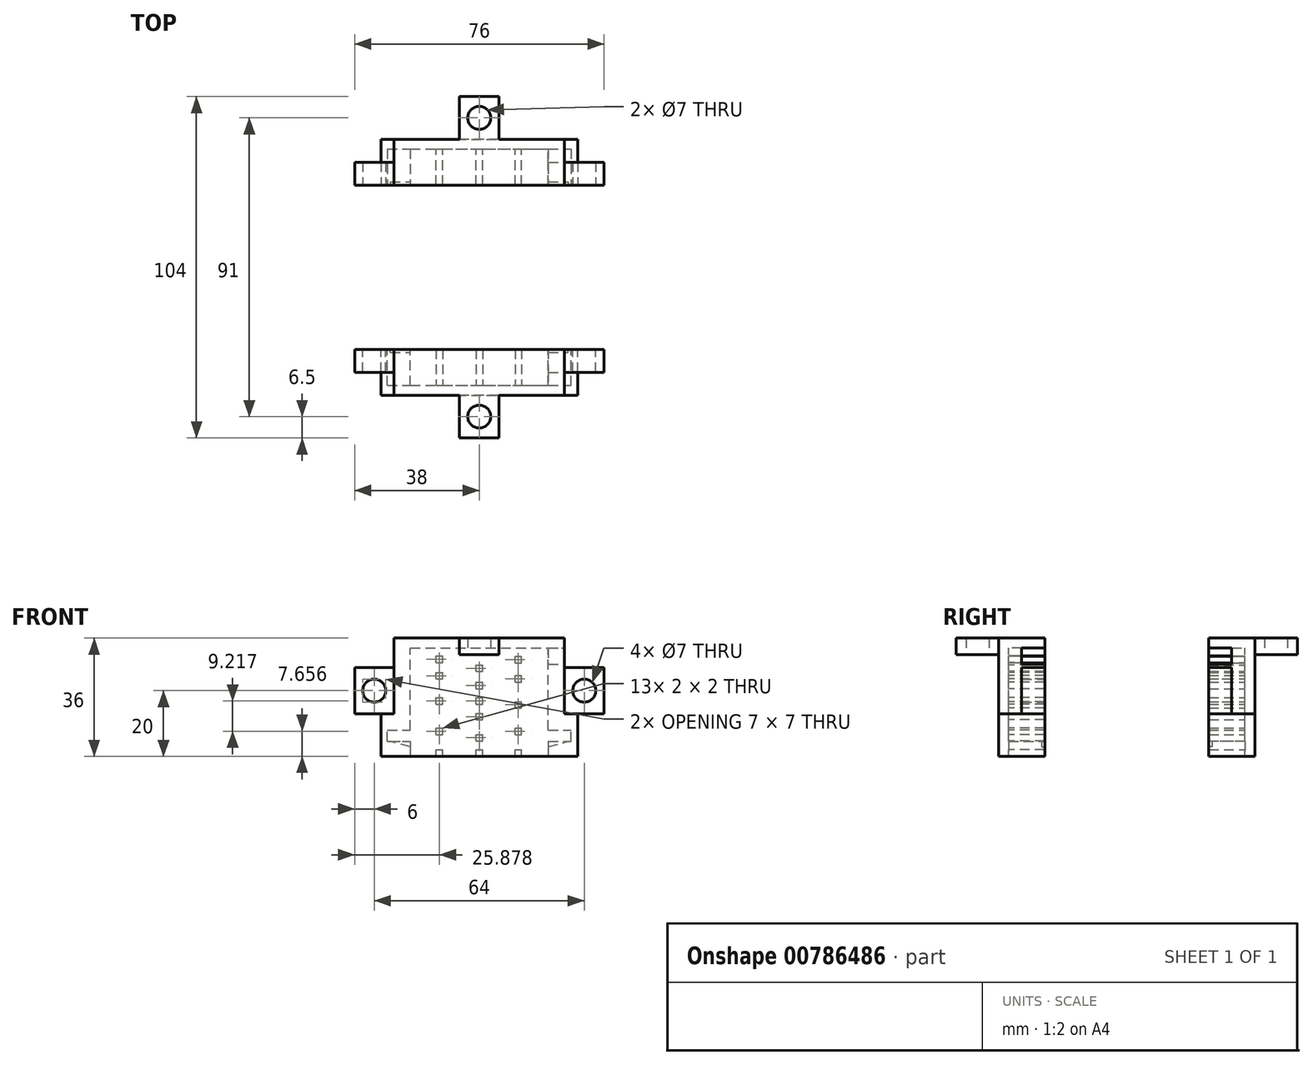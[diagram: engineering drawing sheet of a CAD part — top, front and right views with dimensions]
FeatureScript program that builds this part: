
annotation { "Feature Type Name" : "Feature", "Feature Type Description" : "" }
export const myFeature = defineFeature(function(context is Context, id is Id, definition is map)
    precondition{}
    {
        {
            var Q0;
            Q0=qCreatedBy(makeId("Top.planeOp"),FACE);
            var sketch = newSketch(context, id + "F0", { "sketchPlane" : qUnion([Q0])});
            skLineSegment(sketch, "E0.bottom", {"start": v(-30, 7) * mm, "end": v(30, 7) * mm});
            skLineSegment(sketch, "E0.top", {"start": v(-30, -7) * mm, "end": v(30, -7) * mm});
            skLineSegment(sketch, "E0.left", {"start": v(-30, 7) * mm, "end": v(-30, -7) * mm});
            skLineSegment(sketch, "E0.right", {"start": v(30, 7) * mm, "end": v(30, -7) * mm});
            skSolve(sketch);
        }
        {
            var Q0;
            Q0 = qSketchRegion(id + "F0", true);
            extrude(context, id + "F1", {"entities" : qUnion([Q0]), "depth" : 36 * mm, "offsetDistance" : 25 * mm});
        }
        {
            var Q0;
            Q0=makeQuery(id+"F1.opExtrude","CAP_FACE",FACE,{"disambiguationData":[OSD([sQuery(id+"F0.wireOp",EDGE,"E0.bottom"),sQuery(id+"F0.wireOp",EDGE,"E0.top"),sQuery(id+"F0.wireOp",EDGE,"E0.left"),sQuery(id+"F0.wireOp",EDGE,"E0.right")])],"isStart":false});
            cPlane(context, id + "F2", {"entities" : qUnion([Q0]), "cplaneType" : CPlaneType.OFFSET, "offset" : 3 * mm, "oppositeDirection" : true, "width" : 150 * mm, "height" : 150 * mm});
        }
        {
            var Q0;
            Q0=qCreatedBy(id+"F2.planeOp",FACE);
            var sketch = newSketch(context, id + "F3", { "sketchPlane" : qUnion([Q0])});
            skLineSegment(sketch, "E1.bottom", {"start": v(-21, 7) * mm, "end": v(21, 7) * mm});
            skLineSegment(sketch, "E1.top", {"start": v(-21, -4) * mm, "end": v(21, -4) * mm});
            skLineSegment(sketch, "E1.left", {"start": v(-21, 7) * mm, "end": v(-21, -4) * mm});
            skLineSegment(sketch, "E1.right", {"start": v(21, 7) * mm, "end": v(21, -4) * mm});
            skSolve(sketch);
        }
        {
            var Q0;
            Q0 = qSketchRegion(id + "F3", true);
            extrude(context, id + "F4", {"entities" : qUnion([Q0]), "operationType" : NewBodyOperationType.REMOVE, "oppositeDirection" : true, "depth" : 25 * mm, "offsetDistance" : 25 * mm});
        }
        {
            var Q0;
            Q0=makeQuery(id+"F1.opExtrude","SWEPT_FACE",FACE,{"disambiguationData":[OSD([sQuery(id+"F0.wireOp",EDGE,"E0.bottom")])]});
            var sketch = newSketch(context, id + "F5", { "sketchPlane" : qUnion([Q0])});
            skLineSegment(sketch, "E2.bottom", {"start": v(28, 4.5) * mm, "end": v(-28, 4.5) * mm});
            skLineSegment(sketch, "E2.top", {"start": v(28, 8) * mm, "end": v(-28, 8) * mm});
            skLineSegment(sketch, "E2.left", {"start": v(28, 4.5) * mm, "end": v(28, 8) * mm});
            skLineSegment(sketch, "E2.right", {"start": v(-28, 4.5) * mm, "end": v(-28, 8) * mm});
            skLineSegment(sketch, "E3.bottom", {"start": v(21, 4.5) * mm, "end": v(-21, 4.5) * mm});
            skLineSegment(sketch, "E3.top", {"start": v(21, 0) * mm, "end": v(-21, 0) * mm});
            skLineSegment(sketch, "E3.left", {"start": v(21, 4.5) * mm, "end": v(21, 0) * mm});
            skLineSegment(sketch, "E3.right", {"start": v(-21, 4.5) * mm, "end": v(-21, 0) * mm});
            skSolve(sketch);
        }
        {
            var Q0;
            {var subQ9=sQuery(id+"F5.wireOp",EDGE,"E2.left");Q0=qUnion([makeQuery(id+"F5.imprint","IMPRINT",FACE,{"disambiguationData":[TD([[makeQuery(id+"F5.imprint","IMPRINT",EDGE,{"derivedFrom":subQ9}),1.0]])]}),makeQuery(id+"F5.imprint","IMPRINT",FACE,{"disambiguationData":[TD([[makeQuery(id+"F5.imprint","IMPRINT",EDGE,{"derivedFrom":sQuery(id+"F5.wireOp",EDGE,"E3.top")}),-1.0]])]})]);}
            extrude(context, id + "F6", {"entities" : qUnion([Q0]), "operationType" : NewBodyOperationType.REMOVE, "oppositeDirection" : true, "depth" : 11 * mm, "offsetDistance" : 25 * mm});
        }
        {
            var Q0;
            Q0=makeQuery(id+"F1.opExtrude","SWEPT_FACE",FACE,{"disambiguationData":[OSD([sQuery(id+"F0.wireOp",EDGE,"E0.bottom")])]});
            var sketch = newSketch(context, id + "F7", { "sketchPlane" : qUnion([Q0])});
            skLineSegment(sketch, "E4.bottom", {"start": v(30, 13) * mm, "end": v(38, 13) * mm});
            skLineSegment(sketch, "E4.top", {"start": v(30, 27) * mm, "end": v(38, 27) * mm});
            skLineSegment(sketch, "E4.left", {"start": v(30, 13) * mm, "end": v(30, 27) * mm});
            skLineSegment(sketch, "E4.right", {"start": v(38, 13) * mm, "end": v(38, 27) * mm});
            skLineSegment(sketch, "E5.MirrorCS", {"start": v(-38, 13) * mm, "end": v(-38, 27) * mm});
            skLineSegment(sketch, "E6.MirrorCS", {"start": v(-30, 13) * mm, "end": v(-38, 13) * mm});
            skLineSegment(sketch, "E7.MirrorCS", {"start": v(-30, 13) * mm, "end": v(-30, 27) * mm});
            skLineSegment(sketch, "E8.MirrorCS", {"start": v(-30, 27) * mm, "end": v(-38, 27) * mm});
            skSolve(sketch);
        }
        {
            var Q0;
            Q0 = qSketchRegion(id + "F7", true);
            extrude(context, id + "F8", {"entities" : qUnion([Q0]), "operationType" : NewBodyOperationType.ADD, "oppositeDirection" : true, "depth" : 14 * mm, "offsetDistance" : 25 * mm});
        }
        {
            var Q0;
            Q0=makeQuery(id+"F8.boolean.opBoolean","MERGE",FACE,{"derivedFrom":[makeQuery(id+"F1.opExtrude","SWEPT_FACE",FACE,{"disambiguationData":[OSD([sQuery(id+"F0.wireOp",EDGE,"E0.bottom")])]}),makeQuery(id+"F8.opExtrude","CAP_FACE",FACE,{"disambiguationData":[OSD([sQuery(id+"F7.wireOp",EDGE,"E4.bottom"),sQuery(id+"F7.wireOp",EDGE,"E4.top"),sQuery(id+"F7.wireOp",EDGE,"E4.left"),sQuery(id+"F7.wireOp",EDGE,"E4.right")])],"isStart":true}),makeQuery(id+"F8.opExtrude","CAP_FACE",FACE,{"disambiguationData":[OSD([sQuery(id+"F7.wireOp",EDGE,"E5.MirrorCS"),sQuery(id+"F7.wireOp",EDGE,"E6.MirrorCS"),sQuery(id+"F7.wireOp",EDGE,"E7.MirrorCS"),sQuery(id+"F7.wireOp",EDGE,"E8.MirrorCS")])],"isStart":true})]});
            var sketch = newSketch(context, id + "F9", { "sketchPlane" : qUnion([Q0])});
            skCircle(sketch, "E9", {"center": v(32, 20) * mm, "radius": 3.5 * mm});
            skCircle(sketch, "E10.MirrorC", {"center": v(-32, 20) * mm, "radius": 3.5 * mm});
            skSolve(sketch);
        }
        {
            var Q0;
            Q0 = qSketchRegion(id + "F9", true);
            extrude(context, id + "F10", {"entities" : qUnion([Q0]), "operationType" : NewBodyOperationType.REMOVE, "oppositeDirection" : true, "depth" : 14 * mm, "offsetDistance" : 25 * mm});
        }
        {
            var Q0;
            Q0=makeQuery(id+"F8.boolean.opBoolean","MERGE",FACE,{"derivedFrom":[makeQuery(id+"F1.opExtrude","SWEPT_FACE",FACE,{"disambiguationData":[OSD([sQuery(id+"F0.wireOp",EDGE,"E0.top")])]}),makeQuery(id+"F8.opExtrude","CAP_FACE",FACE,{"disambiguationData":[OSD([sQuery(id+"F7.wireOp",EDGE,"E4.bottom"),sQuery(id+"F7.wireOp",EDGE,"E4.top"),sQuery(id+"F7.wireOp",EDGE,"E4.left"),sQuery(id+"F7.wireOp",EDGE,"E4.right")])],"isStart":false}),makeQuery(id+"F8.opExtrude","CAP_FACE",FACE,{"disambiguationData":[OSD([sQuery(id+"F7.wireOp",EDGE,"E5.MirrorCS"),sQuery(id+"F7.wireOp",EDGE,"E6.MirrorCS"),sQuery(id+"F7.wireOp",EDGE,"E7.MirrorCS"),sQuery(id+"F7.wireOp",EDGE,"E8.MirrorCS")])],"isStart":false})]});
            var sketch = newSketch(context, id + "F11", { "sketchPlane" : qUnion([Q0])});
            skLineSegment(sketch, "E11.bottom", {"start": v(38, 13) * mm, "end": v(26, 13) * mm});
            skLineSegment(sketch, "E11.top", {"start": v(38, 27) * mm, "end": v(26, 27) * mm});
            skLineSegment(sketch, "E11.left", {"start": v(38, 13) * mm, "end": v(38, 27) * mm});
            skLineSegment(sketch, "E11.right", {"start": v(26, 13) * mm, "end": v(26, 27) * mm});
            skLineSegment(sketch, "E12.MirrorCS", {"start": v(-38, 13) * mm, "end": v(-26, 13) * mm});
            skLineSegment(sketch, "E13.MirrorCS", {"start": v(-26, 13) * mm, "end": v(-26, 27) * mm});
            skLineSegment(sketch, "E14.MirrorCS", {"start": v(-38, 13) * mm, "end": v(-38, 27) * mm});
            skLineSegment(sketch, "E15.MirrorCS", {"start": v(-38, 27) * mm, "end": v(-26, 27) * mm});
            skSolve(sketch);
        }
        {
            var Q0;
            Q0 = qSketchRegion(id + "F11", true);
            extrude(context, id + "F12", {"entities" : qUnion([Q0]), "operationType" : NewBodyOperationType.REMOVE, "oppositeDirection" : true, "depth" : 7 * mm, "offsetDistance" : 25 * mm});
        }
        {
            var Q0;
            Q0=makeQuery(id+"F8.boolean.opBoolean","MERGE",FACE,{"derivedFrom":[makeQuery(id+"F1.opExtrude","SWEPT_FACE",FACE,{"disambiguationData":[OSD([sQuery(id+"F0.wireOp",EDGE,"E0.top")])]}),makeQuery(id+"F8.opExtrude","CAP_FACE",FACE,{"disambiguationData":[OSD([sQuery(id+"F7.wireOp",EDGE,"E4.bottom"),sQuery(id+"F7.wireOp",EDGE,"E4.top"),sQuery(id+"F7.wireOp",EDGE,"E4.left"),sQuery(id+"F7.wireOp",EDGE,"E4.right")])],"isStart":false}),makeQuery(id+"F8.opExtrude","CAP_FACE",FACE,{"disambiguationData":[OSD([sQuery(id+"F7.wireOp",EDGE,"E5.MirrorCS"),sQuery(id+"F7.wireOp",EDGE,"E6.MirrorCS"),sQuery(id+"F7.wireOp",EDGE,"E7.MirrorCS"),sQuery(id+"F7.wireOp",EDGE,"E8.MirrorCS")])],"isStart":false})]});
            var sketch = newSketch(context, id + "F13", { "sketchPlane" : qUnion([Q0])});
            skLineSegment(sketch, "E16.bottom", {"start": v(30, 36) * mm, "end": v(26, 36) * mm});
            skLineSegment(sketch, "E16.top", {"start": v(30, 27) * mm, "end": v(26, 27) * mm});
            skLineSegment(sketch, "E16.left", {"start": v(30, 36) * mm, "end": v(30, 27) * mm});
            skLineSegment(sketch, "E16.right", {"start": v(26, 36) * mm, "end": v(26, 27) * mm});
            skLineSegment(sketch, "E17.bottom", {"start": v(-30, 36) * mm, "end": v(-26, 36) * mm});
            skLineSegment(sketch, "E17.top", {"start": v(-30, 27) * mm, "end": v(-26, 27) * mm});
            skLineSegment(sketch, "E17.left", {"start": v(-30, 36) * mm, "end": v(-30, 27) * mm});
            skLineSegment(sketch, "E17.right", {"start": v(-26, 36) * mm, "end": v(-26, 27) * mm});
            skSolve(sketch);
        }
        {
            var Q0;
            Q0 = qSketchRegion(id + "F13", true);
            extrude(context, id + "F14", {"entities" : qUnion([Q0]), "operationType" : NewBodyOperationType.REMOVE, "oppositeDirection" : true, "depth" : 14 * mm, "offsetDistance" : 25 * mm});
        }
        {
            var Q0;
            Q0=makeQuery(id+"F14.boolean.opBoolean","MERGE",FACE,{"derivedFrom":[makeQuery(id+"F12.boolean.opBoolean","COPY",FACE,{"derivedFrom":makeQuery(id+"F12.opExtrude","SWEPT_FACE",FACE,{"disambiguationData":[OSD([sQuery(id+"F11.wireOp",EDGE,"E11.right")])]})}),makeQuery(id+"F14.opExtrude","SWEPT_FACE",FACE,{"disambiguationData":[OSD([sQuery(id+"F13.wireOp",EDGE,"E16.right")])]})]});
            var sketch = newSketch(context, id + "F15", { "sketchPlane" : qUnion([Q0])});
            skLineSegment(sketch, "E18.bottom", {"start": v(7, 33) * mm, "end": v(0, 33) * mm});
            skLineSegment(sketch, "E18.top", {"start": v(7, 28) * mm, "end": v(0, 28) * mm});
            skLineSegment(sketch, "E18.left", {"start": v(7, 33) * mm, "end": v(7, 28) * mm});
            skLineSegment(sketch, "E18.right", {"start": v(0, 33) * mm, "end": v(0, 28) * mm});
            skSolve(sketch);
        }
        {
            var Q0;
            Q0 = qSketchRegion(id + "F15", true);
            extrude(context, id + "F16", {"entities" : qUnion([Q0]), "operationType" : NewBodyOperationType.REMOVE, "oppositeDirection" : true, "depth" : 5 * mm, "offsetDistance" : 25 * mm});
        }
        {
            var Q0;
            {var subQ0=sQuery(id+"F7.wireOp",EDGE,"E8.MirrorCS");var subQ1=sQuery(id+"F7.wireOp",EDGE,"E5.MirrorCS");var subQ3=sQuery(id+"F0.wireOp",EDGE,"E0.bottom");var subQ4=makeQuery(id+"F1.opExtrude","SWEPT_FACE",FACE,{"disambiguationData":[OSD([subQ3])]});var subQ10=sQuery(id+"F0.wireOp",EDGE,"E0.right");var subQ11=sQuery(id+"F7.wireOp",EDGE,"E6.MirrorCS");Q0=makeQuery(id+"F16.boolean.opBoolean","SPLIT",FACE,{"disambiguationData":[TD([makeQuery(id+"F1.opExtrude","SWEPT_FACE",FACE,{"disambiguationData":[OSD([subQ10])]})])],"derivedFrom":makeQuery(id+"F8.boolean.opBoolean","MERGE",FACE,{"derivedFrom":[subQ4,makeQuery(id+"F8.opExtrude","CAP_FACE",FACE,{"disambiguationData":[OSD([sQuery(id+"F7.wireOp",EDGE,"E4.bottom"),sQuery(id+"F7.wireOp",EDGE,"E4.top"),sQuery(id+"F7.wireOp",EDGE,"E4.left"),sQuery(id+"F7.wireOp",EDGE,"E4.right")])],"isStart":true}),makeQuery(id+"F8.opExtrude","CAP_FACE",FACE,{"disambiguationData":[OSD([subQ1,subQ11,sQuery(id+"F7.wireOp",EDGE,"E7.MirrorCS"),subQ0])],"isStart":true})]})});}
            var sketch = newSketch(context, id + "F17", { "sketchPlane" : qUnion([Q0])});
            skLineSegment(sketch, "E19", {"start": v(-21, 2.86) * mm, "end": v(-27.1, 4.5) * mm});
            skLineSegment(sketch, "E20", {"start": v(-27.1, 4.5) * mm, "end": v(-21, 4.5) * mm});
            skLineSegment(sketch, "E21", {"start": v(-21, 4.5) * mm, "end": v(-21, 2.86) * mm});
            skLineSegment(sketch, "E22.MirrorCS", {"start": v(21, 2.86) * mm, "end": v(27.1, 4.5) * mm});
            skLineSegment(sketch, "E23.MirrorCS", {"start": v(21, 4.5) * mm, "end": v(21, 2.86) * mm});
            skLineSegment(sketch, "E24.MirrorCS", {"start": v(27.1, 4.5) * mm, "end": v(21, 4.5) * mm});
            skSolve(sketch);
        }
        {
            var Q0;
            Q0 = qSketchRegion(id + "F17", true);
            extrude(context, id + "F18", {"entities" : qUnion([Q0]), "operationType" : NewBodyOperationType.REMOVE, "oppositeDirection" : true, "depth" : 1 * mm, "offsetDistance" : 25 * mm});
        }
        {
            var Q0;
            Q0=makeQuery(id+"F8.boolean.opBoolean","MERGE",FACE,{"derivedFrom":[makeQuery(id+"F1.opExtrude","SWEPT_FACE",FACE,{"disambiguationData":[OSD([sQuery(id+"F0.wireOp",EDGE,"E0.top")])]}),makeQuery(id+"F8.opExtrude","CAP_FACE",FACE,{"disambiguationData":[OSD([sQuery(id+"F7.wireOp",EDGE,"E4.bottom"),sQuery(id+"F7.wireOp",EDGE,"E4.top"),sQuery(id+"F7.wireOp",EDGE,"E4.left"),sQuery(id+"F7.wireOp",EDGE,"E4.right")])],"isStart":false}),makeQuery(id+"F8.opExtrude","CAP_FACE",FACE,{"disambiguationData":[OSD([sQuery(id+"F7.wireOp",EDGE,"E5.MirrorCS"),sQuery(id+"F7.wireOp",EDGE,"E6.MirrorCS"),sQuery(id+"F7.wireOp",EDGE,"E7.MirrorCS"),sQuery(id+"F7.wireOp",EDGE,"E8.MirrorCS")])],"isStart":false})]});
            var sketch = newSketch(context, id + "F19", { "sketchPlane" : qUnion([Q0])});
            skLineSegment(sketch, "E25.bottom", {"start": v(6, 36) * mm, "end": v(-6, 36) * mm});
            skLineSegment(sketch, "E25.top", {"start": v(6, 31) * mm, "end": v(-6, 31) * mm});
            skLineSegment(sketch, "E25.left", {"start": v(6, 36) * mm, "end": v(6, 31) * mm});
            skLineSegment(sketch, "E25.right", {"start": v(-6, 36) * mm, "end": v(-6, 31) * mm});
            skSolve(sketch);
        }
        {
            var Q0;
            Q0 = qSketchRegion(id + "F19", true);
            extrude(context, id + "F20", {"entities" : qUnion([Q0]), "operationType" : NewBodyOperationType.ADD, "depth" : 13 * mm, "offsetDistance" : 25 * mm});
        }
        {
            var Q0;
            Q0=makeQuery(id+"F20.opExtrude","SWEPT_FACE",FACE,{"disambiguationData":[OSD([sQuery(id+"F19.wireOp",EDGE,"E25.top")])]});
            var sketch = newSketch(context, id + "F21", { "sketchPlane" : qUnion([Q0])});
            skCircle(sketch, "E26", {"center": v(0, 13.5) * mm, "radius": 3.5 * mm});
            skPoint(sketch, "E26.centerSnap0", {"position": v(6, 13.5) * mm});
            skSolve(sketch);
        }
        {
            var Q0;
            Q0 = qSketchRegion(id + "F21", true);
            extrude(context, id + "F22", {"entities" : qUnion([Q0]), "operationType" : NewBodyOperationType.REMOVE, "oppositeDirection" : true, "depth" : 5 * mm, "offsetDistance" : 25 * mm});
        }
        {
            var Q0;
            {var subQ0=sQuery(id+"F7.wireOp",EDGE,"E8.MirrorCS");var subQ1=sQuery(id+"F7.wireOp",EDGE,"E5.MirrorCS");var subQ3=sQuery(id+"F0.wireOp",EDGE,"E0.bottom");var subQ4=makeQuery(id+"F1.opExtrude","SWEPT_FACE",FACE,{"disambiguationData":[OSD([subQ3])]});var subQ10=sQuery(id+"F0.wireOp",EDGE,"E0.right");var subQ11=sQuery(id+"F7.wireOp",EDGE,"E6.MirrorCS");Q0=makeQuery(id+"F16.boolean.opBoolean","SPLIT",FACE,{"disambiguationData":[TD([makeQuery(id+"F1.opExtrude","SWEPT_FACE",FACE,{"disambiguationData":[OSD([subQ10])]})])],"derivedFrom":makeQuery(id+"F8.boolean.opBoolean","MERGE",FACE,{"derivedFrom":[subQ4,makeQuery(id+"F8.opExtrude","CAP_FACE",FACE,{"disambiguationData":[OSD([sQuery(id+"F7.wireOp",EDGE,"E4.bottom"),sQuery(id+"F7.wireOp",EDGE,"E4.top"),sQuery(id+"F7.wireOp",EDGE,"E4.left"),sQuery(id+"F7.wireOp",EDGE,"E4.right")])],"isStart":true}),makeQuery(id+"F8.opExtrude","CAP_FACE",FACE,{"disambiguationData":[OSD([subQ1,subQ11,sQuery(id+"F7.wireOp",EDGE,"E7.MirrorCS"),subQ0])],"isStart":true})]})});}
            cPlane(context, id + "F23", {"entities" : qUnion([Q0]), "cplaneType" : CPlaneType.OFFSET, "offset" : 25 * mm, "width" : 150 * mm, "height" : 150 * mm});
        }
        {
            var Q0;
            Q0=makeQuery(id+"F1.opExtrude","SWEPT_BODY",BODY,{"disambiguationData":[OSD([sQuery(id+"F0.wireOp",EDGE,"E0.bottom"),sQuery(id+"F0.wireOp",EDGE,"E0.top"),sQuery(id+"F0.wireOp",EDGE,"E0.left"),sQuery(id+"F0.wireOp",EDGE,"E0.right")])]});
            var Q1;
            Q1=qCreatedBy(id+"F23.planeOp",FACE);
            mirror(context, id + "F24", {"entities" : qUnion([Q0]), "mirrorPlane" : qUnion([Q1])});
        }
        {
            var Q0;
            Q0=makeQuery(id+"F6.boolean.opBoolean","MERGE",FACE,{"derivedFrom":[makeQuery(id+"F4.boolean.opBoolean","COPY",FACE,{"derivedFrom":makeQuery(id+"F4.opExtrude","SWEPT_FACE",FACE,{"disambiguationData":[OSD([sQuery(id+"F3.wireOp",EDGE,"E1.top")])]})})],"fromTools":[makeQuery(id+"F6.opExtrude","CAP_FACE",FACE,{"disambiguationData":[OSD([sQuery(id+"F5.wireOp",EDGE,"E2.bottom"),sQuery(id+"F5.wireOp",EDGE,"E2.top"),sQuery(id+"F5.wireOp",EDGE,"E2.left"),sQuery(id+"F5.wireOp",EDGE,"E2.right"),sQuery(id+"F5.wireOp",EDGE,"E3.top"),sQuery(id+"F5.wireOp",EDGE,"E3.left"),sQuery(id+"F5.wireOp",EDGE,"E3.right")])],"isStart":false})]});
            var sketch = newSketch(context, id + "F25", { "sketchPlane" : qUnion([Q0])});
            skLineSegment(sketch, "E27.bottom", {"start": v(1, 0) * mm, "end": v(-1, 0) * mm});
            skLineSegment(sketch, "E27.top", {"start": v(1, 2) * mm, "end": v(-1, 2) * mm});
            skLineSegment(sketch, "E27.left", {"start": v(1, 0) * mm, "end": v(1, 2) * mm});
            skLineSegment(sketch, "E27.right", {"start": v(-1, 0) * mm, "end": v(-1, 2) * mm});
            skLineSegment(sketch, "E28.bottom", {"start": v(1, 4.66) * mm, "end": v(-1, 4.66) * mm});
            skLineSegment(sketch, "E28.top", {"start": v(1, 6.66) * mm, "end": v(-1, 6.66) * mm});
            skLineSegment(sketch, "E28.left", {"start": v(1, 4.66) * mm, "end": v(1, 6.66) * mm});
            skLineSegment(sketch, "E28.right", {"start": v(-1, 4.66) * mm, "end": v(-1, 6.66) * mm});
            skLineSegment(sketch, "E29.bottom", {"start": v(1, 11.11) * mm, "end": v(-1, 11.11) * mm});
            skLineSegment(sketch, "E29.top", {"start": v(1, 13.11) * mm, "end": v(-1, 13.11) * mm});
            skLineSegment(sketch, "E29.left", {"start": v(1, 11.11) * mm, "end": v(1, 13.11) * mm});
            skLineSegment(sketch, "E29.right", {"start": v(-1, 11.11) * mm, "end": v(-1, 13.11) * mm});
            skLineSegment(sketch, "E30.bottom", {"start": v(1, 15.92) * mm, "end": v(-1, 15.92) * mm});
            skLineSegment(sketch, "E30.top", {"start": v(1, 17.92) * mm, "end": v(-1, 17.92) * mm});
            skLineSegment(sketch, "E30.left", {"start": v(1, 15.92) * mm, "end": v(1, 17.92) * mm});
            skLineSegment(sketch, "E30.right", {"start": v(-1, 15.92) * mm, "end": v(-1, 17.92) * mm});
            skLineSegment(sketch, "E31.bottom", {"start": v(1, 20.57) * mm, "end": v(-1, 20.57) * mm});
            skLineSegment(sketch, "E31.top", {"start": v(1, 22.57) * mm, "end": v(-1, 22.57) * mm});
            skLineSegment(sketch, "E31.left", {"start": v(1, 20.57) * mm, "end": v(1, 22.57) * mm});
            skLineSegment(sketch, "E31.right", {"start": v(-1, 20.57) * mm, "end": v(-1, 22.57) * mm});
            skLineSegment(sketch, "E32.bottom", {"start": v(1, 25.85) * mm, "end": v(-1, 25.85) * mm});
            skLineSegment(sketch, "E32.top", {"start": v(1, 27.85) * mm, "end": v(-1, 27.85) * mm});
            skLineSegment(sketch, "E32.left", {"start": v(1, 25.85) * mm, "end": v(1, 27.85) * mm});
            skLineSegment(sketch, "E32.right", {"start": v(-1, 25.85) * mm, "end": v(-1, 27.85) * mm});
            skLineSegment(sketch, "E33.bottom", {"start": v(13.12, 0) * mm, "end": v(11.12, 0) * mm});
            skLineSegment(sketch, "E33.top", {"start": v(13.12, 2) * mm, "end": v(11.12, 2) * mm});
            skLineSegment(sketch, "E33.left", {"start": v(13.12, 0) * mm, "end": v(13.12, 2) * mm});
            skLineSegment(sketch, "E33.right", {"start": v(11.12, 0) * mm, "end": v(11.12, 2) * mm});
            skLineSegment(sketch, "E34.bottom", {"start": v(13.12, 6.66) * mm, "end": v(11.12, 6.66) * mm});
            skLineSegment(sketch, "E34.top", {"start": v(13.12, 8.66) * mm, "end": v(11.12, 8.66) * mm});
            skLineSegment(sketch, "E34.left", {"start": v(13.12, 6.66) * mm, "end": v(13.12, 8.66) * mm});
            skLineSegment(sketch, "E34.right", {"start": v(11.12, 6.66) * mm, "end": v(11.12, 8.66) * mm});
            skLineSegment(sketch, "E35.bottom", {"start": v(13.12, 15.87) * mm, "end": v(11.12, 15.87) * mm});
            skLineSegment(sketch, "E35.top", {"start": v(13.12, 17.87) * mm, "end": v(11.12, 17.87) * mm});
            skLineSegment(sketch, "E35.left", {"start": v(13.12, 15.87) * mm, "end": v(13.12, 17.87) * mm});
            skLineSegment(sketch, "E35.right", {"start": v(11.12, 15.87) * mm, "end": v(11.12, 17.87) * mm});
            skLineSegment(sketch, "E36.bottom", {"start": v(13.12, 23.55) * mm, "end": v(11.12, 23.55) * mm});
            skLineSegment(sketch, "E36.top", {"start": v(13.12, 25.55) * mm, "end": v(11.12, 25.55) * mm});
            skLineSegment(sketch, "E36.left", {"start": v(13.12, 23.55) * mm, "end": v(13.12, 25.55) * mm});
            skLineSegment(sketch, "E36.right", {"start": v(11.12, 23.55) * mm, "end": v(11.12, 25.55) * mm});
            skLineSegment(sketch, "E37.bottom", {"start": v(13.12, 28.56) * mm, "end": v(11.12, 28.56) * mm});
            skLineSegment(sketch, "E37.top", {"start": v(13.12, 30.56) * mm, "end": v(11.12, 30.56) * mm});
            skLineSegment(sketch, "E37.left", {"start": v(13.12, 28.56) * mm, "end": v(13.12, 30.56) * mm});
            skLineSegment(sketch, "E37.right", {"start": v(11.12, 28.56) * mm, "end": v(11.12, 30.56) * mm});
            skLineSegment(sketch, "E38.bottom", {"start": v(-10.9, 0) * mm, "end": v(-12.9, 0) * mm});
            skLineSegment(sketch, "E38.top", {"start": v(-10.9, 2) * mm, "end": v(-12.9, 2) * mm});
            skLineSegment(sketch, "E38.left", {"start": v(-10.9, 0) * mm, "end": v(-10.9, 2) * mm});
            skLineSegment(sketch, "E38.right", {"start": v(-12.9, 0) * mm, "end": v(-12.9, 2) * mm});
            skLineSegment(sketch, "E39.bottom", {"start": v(-10.9, 6.66) * mm, "end": v(-12.9, 6.66) * mm});
            skLineSegment(sketch, "E39.top", {"start": v(-10.9, 8.66) * mm, "end": v(-12.9, 8.66) * mm});
            skLineSegment(sketch, "E39.left", {"start": v(-10.9, 6.66) * mm, "end": v(-10.9, 8.66) * mm});
            skLineSegment(sketch, "E39.right", {"start": v(-12.9, 6.66) * mm, "end": v(-12.9, 8.66) * mm});
            skLineSegment(sketch, "E40.bottom", {"start": v(-10.9, 14.68) * mm, "end": v(-12.9, 14.68) * mm});
            skLineSegment(sketch, "E40.top", {"start": v(-10.9, 16.68) * mm, "end": v(-12.9, 16.68) * mm});
            skLineSegment(sketch, "E40.left", {"start": v(-10.9, 14.68) * mm, "end": v(-10.9, 16.68) * mm});
            skLineSegment(sketch, "E40.right", {"start": v(-12.9, 14.68) * mm, "end": v(-12.9, 16.68) * mm});
            skLineSegment(sketch, "E41.bottom", {"start": v(-10.9, 22.57) * mm, "end": v(-12.9, 22.57) * mm});
            skLineSegment(sketch, "E41.top", {"start": v(-10.9, 24.57) * mm, "end": v(-12.9, 24.57) * mm});
            skLineSegment(sketch, "E41.left", {"start": v(-10.9, 22.57) * mm, "end": v(-10.9, 24.57) * mm});
            skLineSegment(sketch, "E41.right", {"start": v(-12.9, 22.57) * mm, "end": v(-12.9, 24.57) * mm});
            skLineSegment(sketch, "E42.bottom", {"start": v(-10.9, 28.44) * mm, "end": v(-12.9, 28.44) * mm});
            skLineSegment(sketch, "E42.top", {"start": v(-10.9, 30.44) * mm, "end": v(-12.9, 30.44) * mm});
            skLineSegment(sketch, "E42.left", {"start": v(-10.9, 28.44) * mm, "end": v(-10.9, 30.44) * mm});
            skLineSegment(sketch, "E42.right", {"start": v(-12.9, 28.44) * mm, "end": v(-12.9, 30.44) * mm});
            skSolve(sketch);
        }
        {
            var Q0;
            Q0 = qSketchRegion(id + "F25", true);
            extrude(context, id + "F26", {"entities" : qUnion([Q0]), "operationType" : NewBodyOperationType.ADD, "depth" : 11 * mm, "offsetDistance" : 25 * mm});
        }
        {
            var Q0;
            Q0=makeQuery(id+"F1.opExtrude","SWEPT_BODY",BODY,{"disambiguationData":[OSD([sQuery(id+"F0.wireOp",EDGE,"E0.bottom"),sQuery(id+"F0.wireOp",EDGE,"E0.top"),sQuery(id+"F0.wireOp",EDGE,"E0.left"),sQuery(id+"F0.wireOp",EDGE,"E0.right")])]});
            var Q1;
            Q1=qCreatedBy(id+"F23.planeOp",FACE);
            mirror(context, id + "F27", {"operationType" : NewBodyOperationType.ADD, "entities" : qUnion([Q0]), "mirrorPlane" : qUnion([Q1])});
        }
    });
